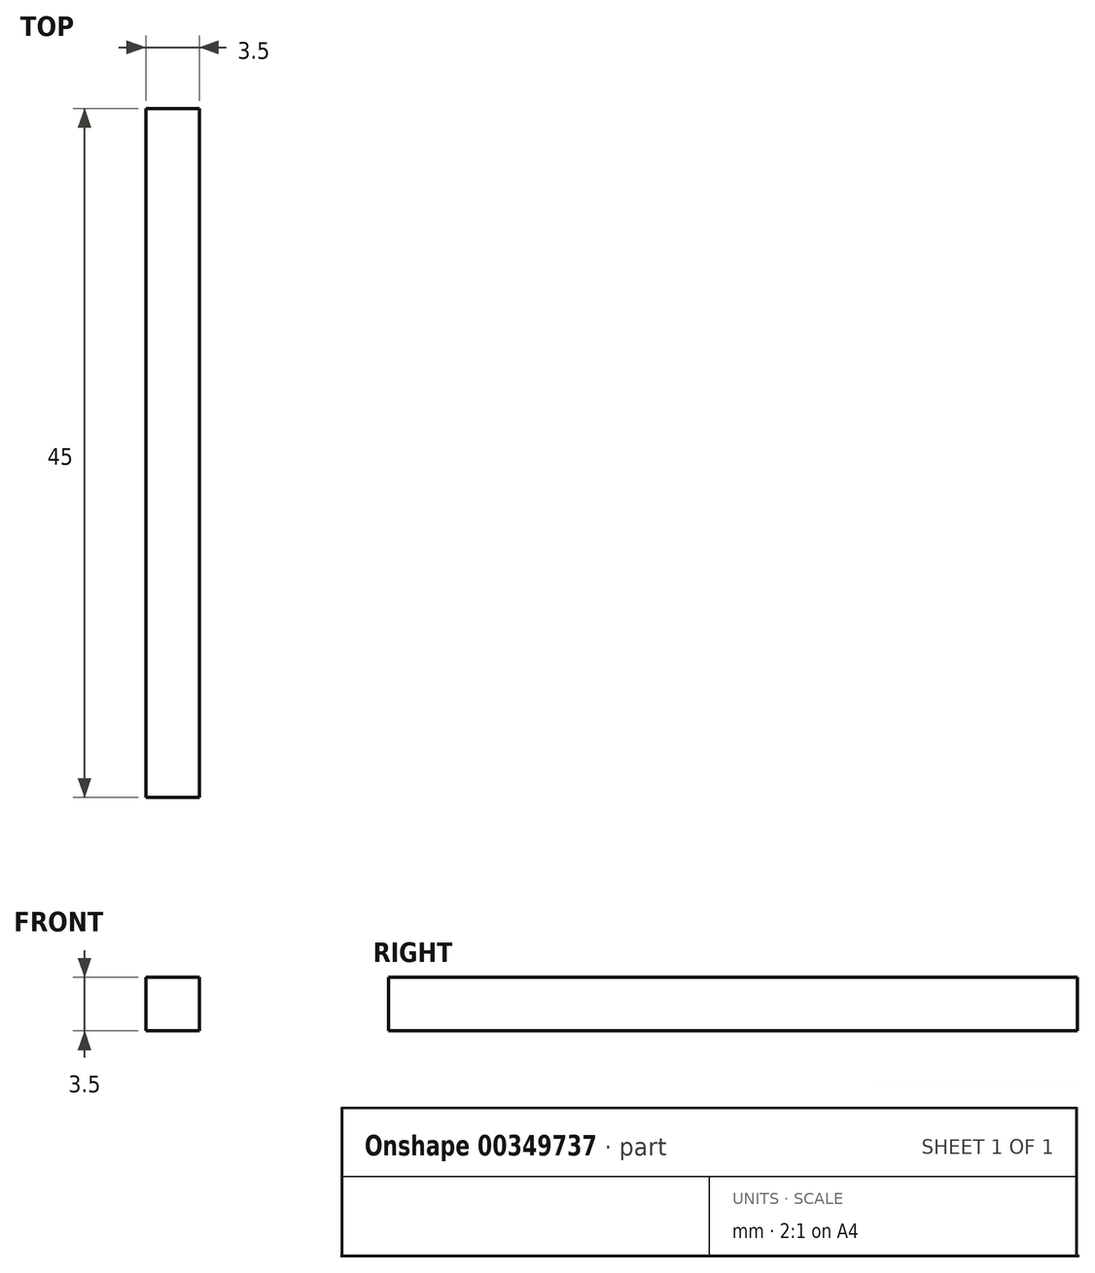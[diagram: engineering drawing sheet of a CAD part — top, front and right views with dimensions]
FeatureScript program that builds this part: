
annotation { "Feature Type Name" : "Feature", "Feature Type Description" : "" }
export const myFeature = defineFeature(function(context is Context, id is Id, definition is map)
    precondition{}
    {
        {
            var Q0;
            Q0=qCreatedBy(makeId("Top.planeOp"),FACE);
            var sketch = newSketch(context, id + "F0", { "sketchPlane" : qUnion([Q0])});
            skLineSegment(sketch, "E0.bottom", {"start": v(1.75, -22.5) * mm, "end": v(-1.75, -22.5) * mm});
            skLineSegment(sketch, "E0.top", {"start": v(1.75, 22.5) * mm, "end": v(-1.75, 22.5) * mm});
            skLineSegment(sketch, "E0.left", {"start": v(1.75, -22.5) * mm, "end": v(1.75, 22.5) * mm});
            skLineSegment(sketch, "E0.right", {"start": v(-1.75, -22.5) * mm, "end": v(-1.75, 22.5) * mm});
            skPoint(sketch, "E0.middle", {"position": v(0, 0) * mm});
            skSolve(sketch);
        }
        {
            var Q0;
            Q0=qSketchRegion(id+"F0",true);
            extrude(context, id + "F1", {"entities" : qUnion([Q0]), "depth" : 3.5 * mm});
        }
    });
